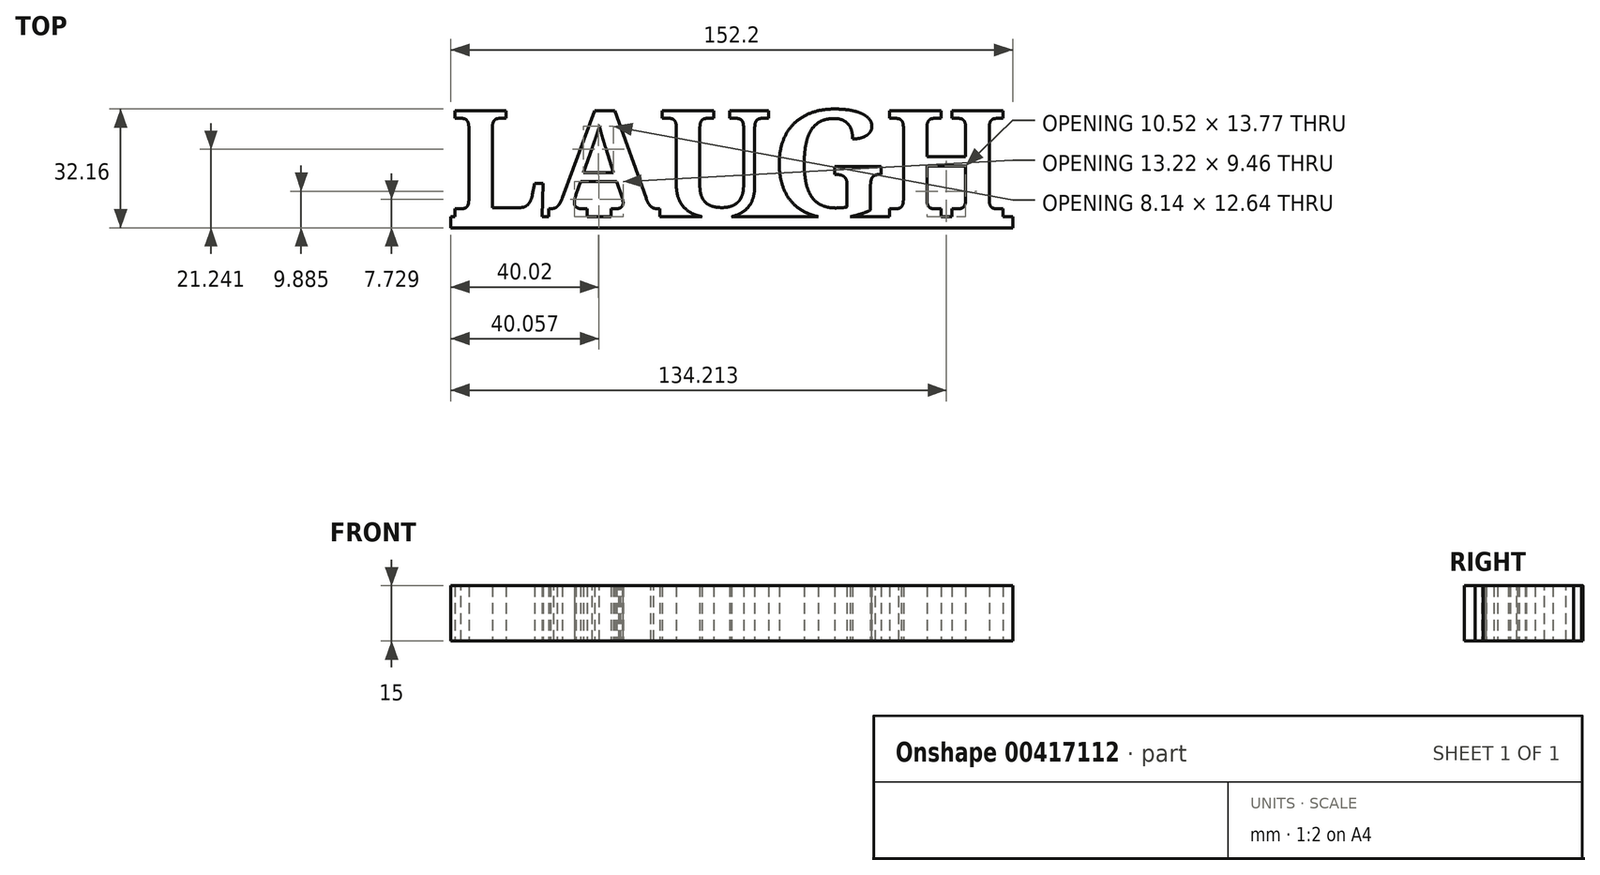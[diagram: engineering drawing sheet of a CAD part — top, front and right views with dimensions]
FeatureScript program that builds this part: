
annotation { "Feature Type Name" : "Feature", "Feature Type Description" : "" }
export const myFeature = defineFeature(function(context is Context, id is Id, definition is map)
    precondition{}
    {
        {
            var Q0;
            Q0=qCreatedBy(makeId("Top.planeOp"),FACE);
            var sketch = newSketch(context, id + "F0", { "sketchPlane" : qUnion([Q0])});
            skText(sketch, "E0", { "text": "LAUGH", "fontName": "NotoSerif-Bold.ttf"});
            skLineSegment(sketch, "E1", {"start": v(0, 0) * mm, "end": v(152.2, 0) * mm});
            skLineSegment(sketch, "E2", {"start": v(152.2, -3) * mm, "end": v(0, -3) * mm});
            skLineSegment(sketch, "E3", {"start": v(0, -3) * mm, "end": v(0, 0) * mm});
            skLineSegment(sketch, "E4", {"start": v(152.2, 0) * mm, "end": v(152.2, -3) * mm});
            const initialGuessF0  = {"E0": [0, 0, 1, 0, 0.029]};
            skSetInitialGuess(sketch, initialGuessF0);
            skSolve(sketch);
        }
        {
            var Q0;
            Q0 = qSketchRegion(id + "F0", true);
            extrude(context, id + "F1", {"entities" : qUnion([Q0]), "depth" : 15 * mm});
        }
    });
